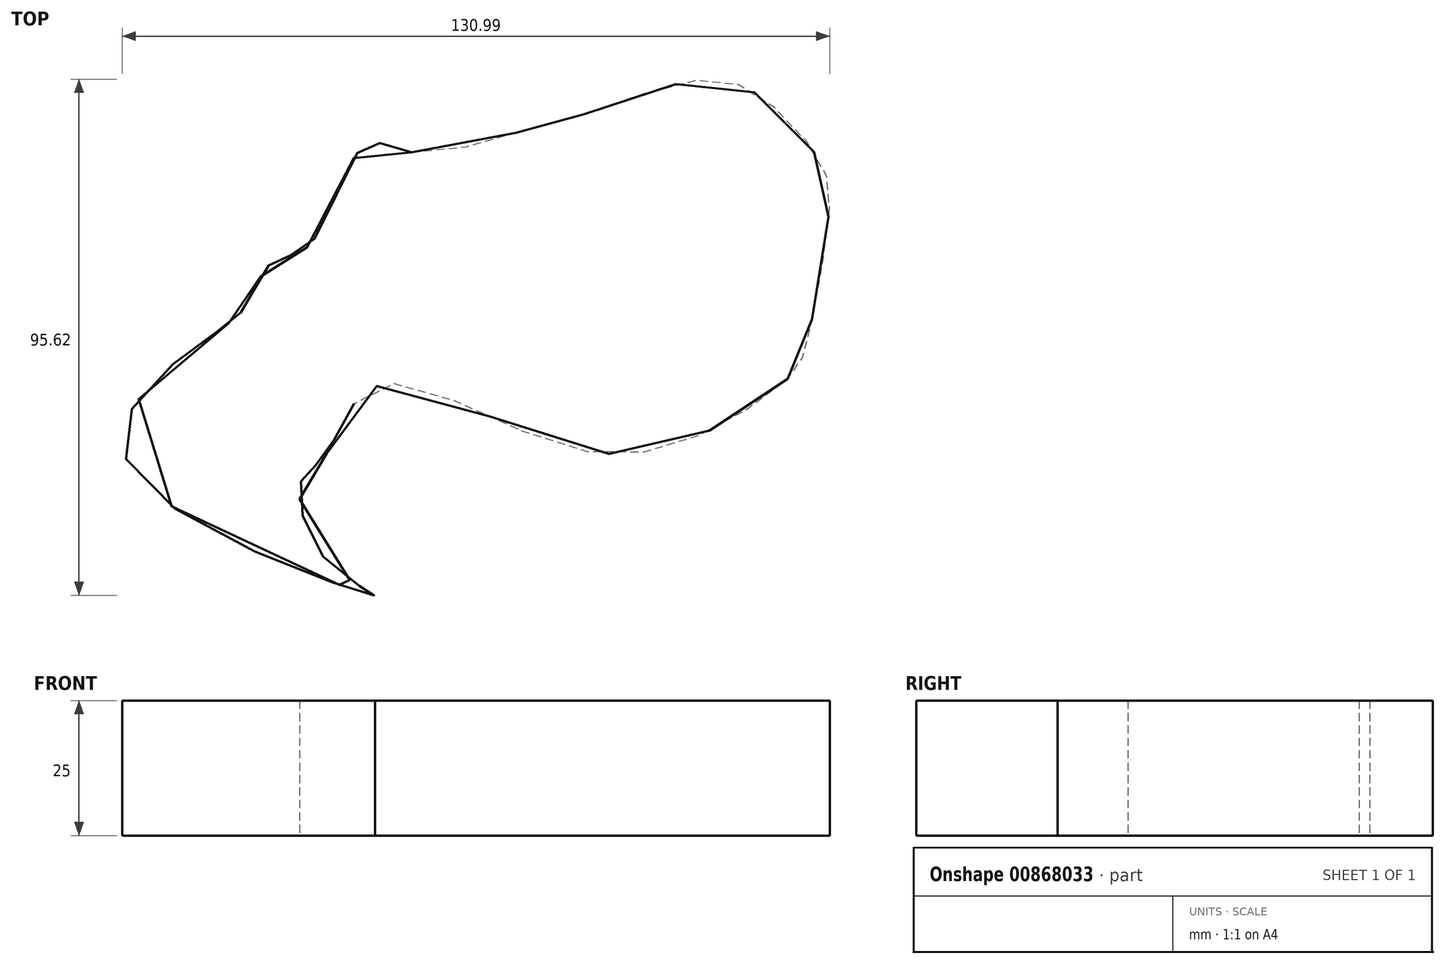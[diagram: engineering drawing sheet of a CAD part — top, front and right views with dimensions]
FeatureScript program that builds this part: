
annotation { "Feature Type Name" : "Feature", "Feature Type Description" : "" }
export const myFeature = defineFeature(function(context is Context, id is Id, definition is map)
    precondition{}
    {
        {
            var Q0;
            Q0=qCreatedBy(makeId("Top.planeOp"),FACE);
            var sketch = newSketch(context, id + "F0", { "sketchPlane" : qUnion([Q0])});
            skFitSpline(sketch, "E0", {"points": [v(-38.35, 24.54) * mm, v(-14.46, 29.58) * mm, v(-5.7, 31.82) * mm, v(15.4, 37.98) * mm, v(27.53, 33.87) * mm, v(37.79, 21.74) * mm, v(38.72, 11.48) * mm, v(34.62, -11.48) * mm, v(31.26, -17.45) * mm, v(13.16, -28.64) * mm, v(-12.6, -29.2) * mm, v(-45.25, -18.94) * mm, v(-54.58, -32) * mm, v(-58.69, -36.1) * mm, v(-53.65, -51.6) * mm, v(-45.25, -57.57) * mm, v(-91.35, -32) * mm, v(-73.8, -8.3) * mm, v(-68.58, -3.08) * mm, v(-63.91, 4.39) * mm, v(-57.38, 7.18) * mm, v(-47.12, 25.85) * mm, v(-38.35, 24.54) * mm]});
            skSolve(sketch);
        }
        {
            var Q0;
            Q0 = qSketchRegion(id + "F0", true);
            var Q1;
            Q1=makeQuery(id+"F0.imprint","IMPRINT",FACE,{"disambiguationData":[TD([[makeQuery(id+"F0.imprint","IMPRINT",EDGE,{"derivedFrom":sQuery(id+"F0.wireOp",EDGE,"E0")}),-1.0]])]});
            extrude(context, id + "F1", {"entities" : qUnion([Q0, Q1]), "depth" : 25 * mm, "offsetDistance" : 25 * mm});
        }
    });
